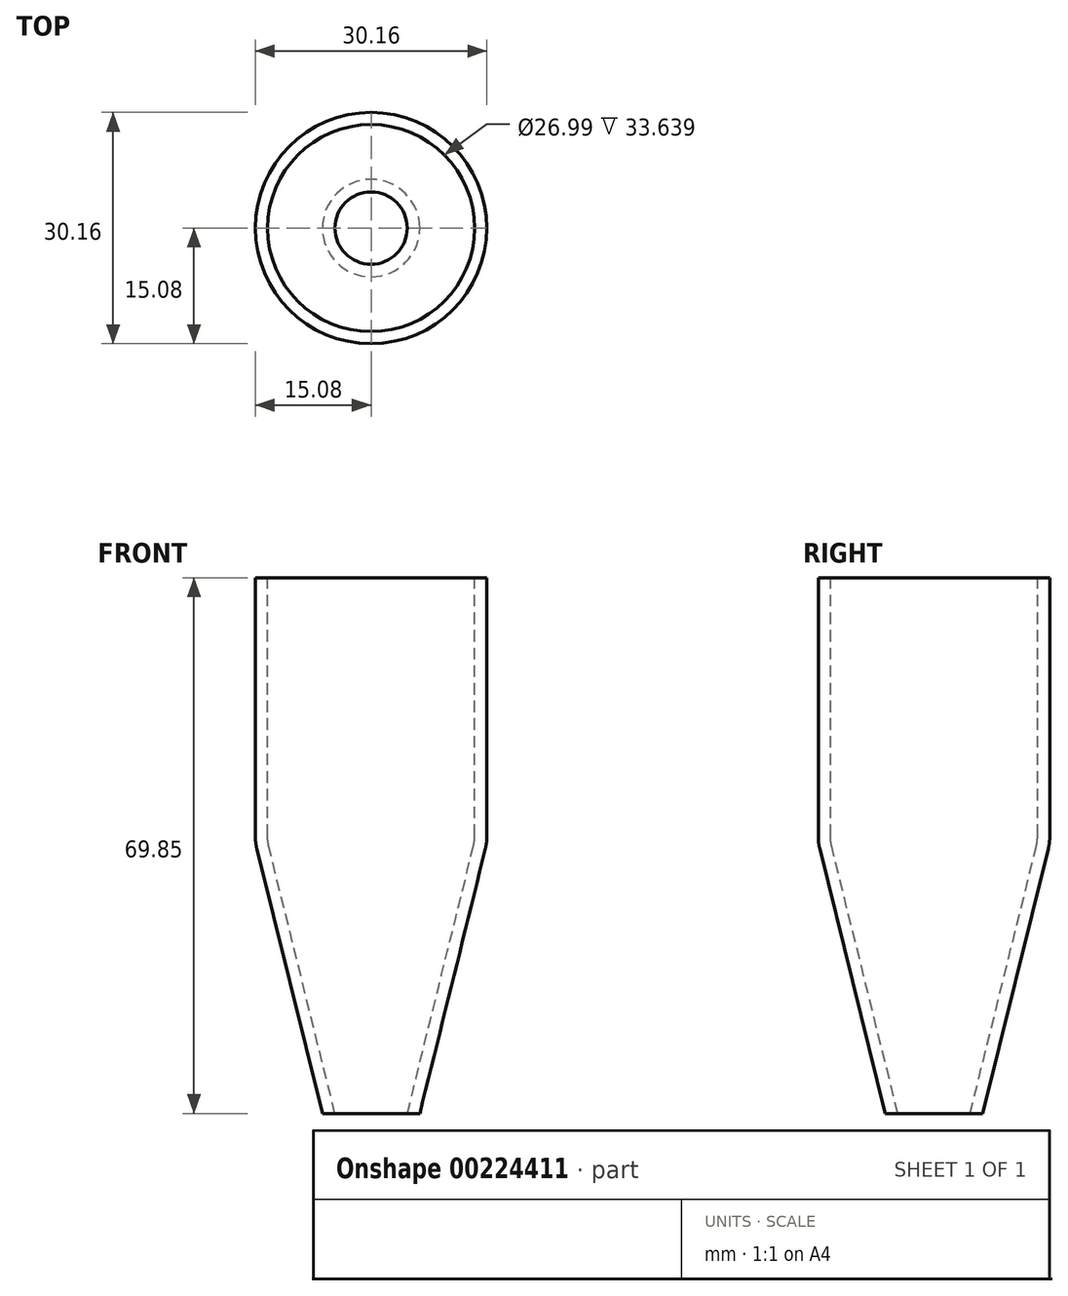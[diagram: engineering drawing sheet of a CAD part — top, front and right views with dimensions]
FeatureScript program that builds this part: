
annotation { "Feature Type Name" : "Feature", "Feature Type Description" : "" }
export const myFeature = defineFeature(function(context is Context, id is Id, definition is map)
    precondition{}
    {
        {
            var Q0;
            Q0=qCreatedBy(makeId("Front.planeOp"),FACE);
            var sketch = newSketch(context, id + "F0", { "sketchPlane" : qUnion([Q0])});
            skLineSegment(sketch, "E0", {"start": v(-15.08, 36.02) * mm, "end": v(-15.08, 69.85) * mm});
            skLineSegment(sketch, "E1", {"start": v(-15.08, 69.85) * mm, "end": v(-13.5, 69.85) * mm});
            skLineSegment(sketch, "E2", {"start": v(-13.5, 69.85) * mm, "end": v(-13.5, 36.21) * mm});
            skLineSegment(sketch, "E3", {"start": v(-14.9, 34.5) * mm, "end": v(-6.35, 0) * mm});
            skLineSegment(sketch, "E4", {"start": v(-6.35, 0) * mm, "end": v(-4.71, 0) * mm});
            skLineSegment(sketch, "E5", {"start": v(-4.71, 0) * mm, "end": v(-13.3, 34.68) * mm});
            skPoint(sketch, "E6.visualSharp", {"position": v(-15.08, 35.24) * mm});
            skArc(sketch, "E6.filletArc", {"start": v(-15.08, 36.02) * mm, "mid": v(-15.03, 35.25) * mm, "end": v(-14.9, 34.5) * mm});
            skPoint(sketch, "E7.visualSharp", {"position": v(-13.5, 35.44) * mm});
            skArc(sketch, "E7.filletArc", {"start": v(-13.5, 36.21) * mm, "mid": v(-13.45, 35.44) * mm, "end": v(-13.3, 34.68) * mm});
            skLineSegment(sketch, "E8", {"start": v(0, 67.36) * mm, "end": v(0, -33.29) * mm, "construction": true});
            skSolve(sketch);
        }
        {
            var Q0;
            Q0=makeQuery(id+"F0.imprint","IMPRINT",FACE,{"disambiguationData":[TD([[makeQuery(id+"F0.imprint","IMPRINT",EDGE,{"derivedFrom":sQuery(id+"F0.wireOp",EDGE,"E0")}),-1.0]])]});
            var Q1;
            Q1=sQuery(id+"F0.wireOp",EDGE,"E8");
            revolve(context, id + "F1", {"entities" : qUnion([Q0]), "axis" : qUnion([Q1]), "revolveType" : RevolveType.FULL});
        }
    });
